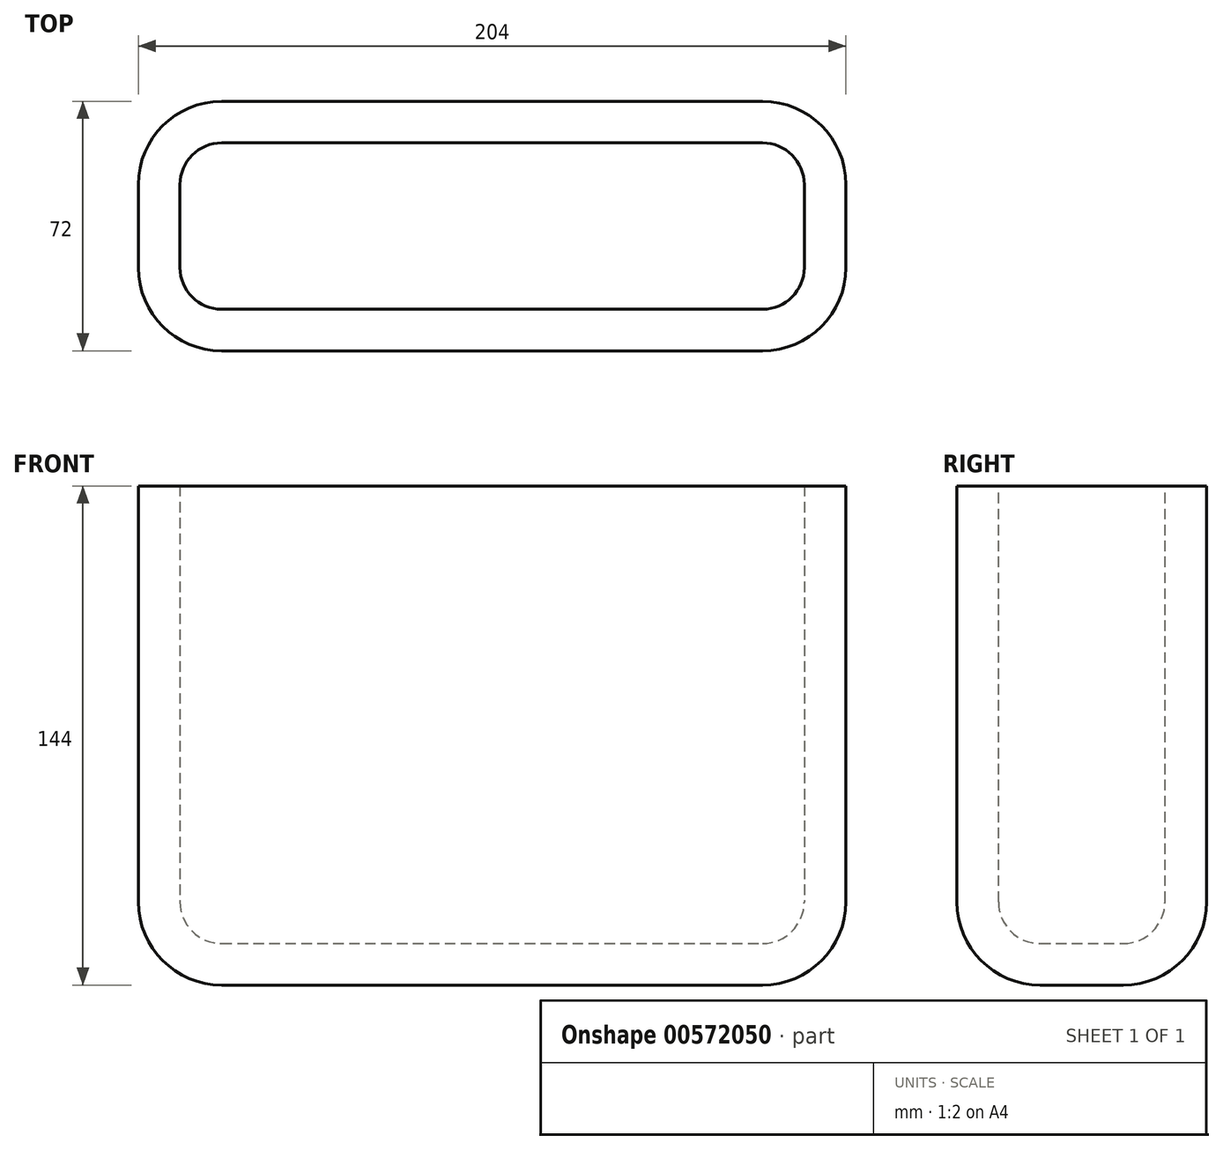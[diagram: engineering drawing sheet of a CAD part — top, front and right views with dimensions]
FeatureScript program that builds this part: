
annotation { "Feature Type Name" : "Feature", "Feature Type Description" : "" }
export const myFeature = defineFeature(function(context is Context, id is Id, definition is map)
    precondition{}
    {
        {
            var Q0;
            Q0=qCreatedBy(makeId("Top.planeOp"),FACE);
            var sketch = newSketch(context, id + "F0", { "sketchPlane" : qUnion([Q0])});
            skLineSegment(sketch, "E0.bottom", {"start": v(-85, 30) * mm, "end": v(85, 30) * mm});
            skLineSegment(sketch, "E0.top", {"start": v(-85, -30) * mm, "end": v(85, -30) * mm});
            skLineSegment(sketch, "E0.left", {"start": v(-85, 30) * mm, "end": v(-85, -30) * mm});
            skLineSegment(sketch, "E0.right", {"start": v(85, 30) * mm, "end": v(85, -30) * mm});
            skPoint(sketch, "E0.middle", {"position": v(0, 0) * mm});
            skSolve(sketch);
        }
        {
            var Q0;
            Q0 = qSketchRegion(id + "F0", true);
            extrude(context, id + "F1", {"entities" : qUnion([Q0]), "endBound" : BoundingType.SYMMETRIC, "depth" : 120 * mm, "offsetDistance" : 25 * mm});
        }
        {
            var Q0;
            Q0=makeQuery(id+"F1.opExtrude","SWEPT_EDGE",EDGE,{"disambiguationData":[OSD([sQuery(id+"F0.wireOp",EDGE,"E0.top"),sQuery(id+"F0.wireOp",EDGE,"E0.left")])]});
            var Q1;
            Q1=makeQuery(id+"F1.opExtrude","SWEPT_EDGE",EDGE,{"disambiguationData":[OSD([sQuery(id+"F0.wireOp",EDGE,"E0.bottom"),sQuery(id+"F0.wireOp",EDGE,"E0.left")])]});
            var Q2;
            Q2=makeQuery(id+"F1.opExtrude","SWEPT_EDGE",EDGE,{"disambiguationData":[OSD([sQuery(id+"F0.wireOp",EDGE,"E0.top"),sQuery(id+"F0.wireOp",EDGE,"E0.right")])]});
            var Q3;
            Q3=makeQuery(id+"F1.opExtrude","SWEPT_EDGE",EDGE,{"disambiguationData":[OSD([sQuery(id+"F0.wireOp",EDGE,"E0.bottom"),sQuery(id+"F0.wireOp",EDGE,"E0.right")])]});
            var Q4;
            Q4=makeQuery(id+"F1.opExtrude","CAP_EDGE",EDGE,{"disambiguationData":[OSD([sQuery(id+"F0.wireOp",EDGE,"E0.bottom")])],"isStart":true});
            var Q5;
            Q5=makeQuery(id+"F1.opExtrude","CAP_EDGE",EDGE,{"disambiguationData":[OSD([sQuery(id+"F0.wireOp",EDGE,"E0.top")])],"isStart":true});
            var Q6;
            Q6=makeQuery(id+"F1.opExtrude","CAP_EDGE",EDGE,{"disambiguationData":[OSD([sQuery(id+"F0.wireOp",EDGE,"E0.left")])],"isStart":true});
            var Q7;
            Q7=makeQuery(id+"F1.opExtrude","CAP_EDGE",EDGE,{"disambiguationData":[OSD([sQuery(id+"F0.wireOp",EDGE,"E0.right")])],"isStart":true});
            fillet(context, id + "F2", {"entities" : qUnion([Q0, Q1, Q2, Q3, Q4, Q5, Q6, Q7]), "radius" : 20 * mm, "tangentPropagation" : true, "allowEdgeOverflow" : false});
        }
        {
            var Q0;
            Q0=makeQuery(id+"F1.opExtrude","CAP_FACE",FACE,{"disambiguationData":[OSD([sQuery(id+"F0.wireOp",EDGE,"E0.bottom"),sQuery(id+"F0.wireOp",EDGE,"E0.top"),sQuery(id+"F0.wireOp",EDGE,"E0.left"),sQuery(id+"F0.wireOp",EDGE,"E0.right")])],"isStart":false});
            shell(context, id + "F3", {"entities" : qUnion([Q0]), "thickness" : 10 * mm});
        }
        {
            var Q0;
            Q0=makeQuery(id+"F1.opExtrude","SWEPT_BODY",BODY,{"disambiguationData":[OSD([sQuery(id+"F0.wireOp",EDGE,"E0.bottom"),sQuery(id+"F0.wireOp",EDGE,"E0.top"),sQuery(id+"F0.wireOp",EDGE,"E0.left"),sQuery(id+"F0.wireOp",EDGE,"E0.right")])]});
            var Q1;
            Q1=qCreatedBy(makeId("Origin.pointOp"),VERTEX);
            transform(context, id + "F4", {"entities" : qUnion([Q0]), "transformType" : TransformType.SCALE_UNIFORMLY, "scale" : 1.2, "scalePoint" : qUnion([Q1]), "makeCopy" : false});
        }
    });
